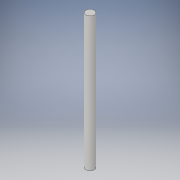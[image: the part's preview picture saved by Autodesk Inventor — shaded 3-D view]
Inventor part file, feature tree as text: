
AUTODESK INVENTOR PART (.ipt)
format: ipt  version: 2019 (Build 230136000, 136)  size: 88,576 bytes
history: native  units: in
note: dims shown in document units (in); Inventor stores cm internally (conversion verified against a paired STEP export)
features: extrude x1, sketch x1
ambient origin geometry x8: Origin, YZ Plane, XZ Plane, XY Plane, X Axis, Y Axis, Z Axis, Center Point
bodies: Solid1 (feature_tree)
feature tree (2):
  extrude  "Extrusion1"  Depth=4.0in TaperAngle=0.0deg
  sketch  "Sketch1"  dims[d0=0.25in d1=4.0in d2=0.0in]
